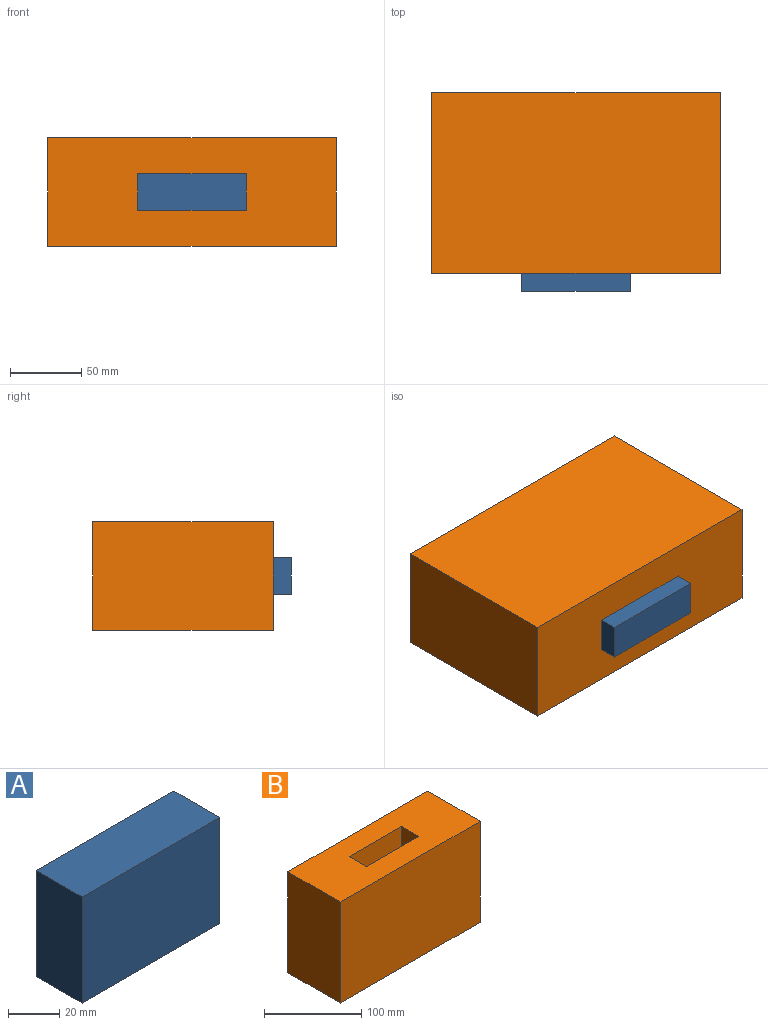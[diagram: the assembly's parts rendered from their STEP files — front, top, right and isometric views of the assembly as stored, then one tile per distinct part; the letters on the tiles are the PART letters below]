
ASSEMBLY  parts=2 mates=1
PART A: 6 faces, bbox 76.2x25.4x50.8 mm
  f0: plane 50.8x25.4mm, normal (1,0,0), area 1290.3mm2, adj f1,f3,f4,f5
  f1: plane 76.2x50.8mm, normal (0,1,0), area 3871mm2, adj f0,f2,f4,f5
  f2: plane 50.8x25.4mm, normal (-1,0,0), area 1290.3mm2, adj f1,f3,f4,f5
  f3: plane 76.2x50.8mm, normal (0,-1,0), area 3871mm2, adj f0,f2,f4,f5
  f4: plane 76.2x25.4mm, normal (0,0,1), area 1935.5mm2, adj f0,f1,f2,f3
  f5: plane 76.2x25.4mm, normal (0,0,-1), area 1935.5mm2, adj f0,f1,f2,f3
PART B: 11 faces, bbox 203.2x76.2x127 mm
  f0: plane 203.2x76.2mm, normal (0,0,1), area 13548.4mm2, adj f1,f2,f3,f4,f6,f7,f8,f9
  f1: plane 127x76.2mm, normal (1,0,0), area 9677.4mm2, adj f0,f2,f4,f5
  f2: plane 203.2x127mm, normal (0,1,0), area 25806.4mm2, adj f0,f1,f3,f5
  f3: plane 127x76.2mm, normal (-1,0,0), area 9677.4mm2, adj f0,f2,f4,f5
  f4: plane 203.2x127mm, normal (0,-1,0), area 25806.4mm2, adj f0,f1,f3,f5
  f5: plane 203.2x76.2mm, normal (0,0,-1), area 15483.8mm2, adj f1,f2,f3,f4
  f6: plane 25.4x25.4mm, normal (-1,0,0), area 645.2mm2, adj f0,f7,f9,f10
  f7: plane 76.2x25.4mm, normal (0,-1,0), area 1935.5mm2, adj f0,f6,f8,f10
  f8: plane 25.4x25.4mm, normal (1,0,0), area 645.2mm2, adj f0,f7,f9,f10
  f9: plane 76.2x25.4mm, normal (0,1,0), area 1935.5mm2, adj f0,f6,f8,f10
  f10: plane 76.2x25.4mm, normal (0,0,1), area 1935.5mm2, adj f6,f7,f8,f9
PLACE A rot(axis=(1,0,0),90deg) t=(0,-25.4,-38.1)mm
PLACE B rot(axis=(1,0,0),90deg) t=(0,63.5,-38.1)mm
MATE fastened A.f3 <-> B.f9  axis (0,0,-1) through (0,-50.8,-50.8)mm
